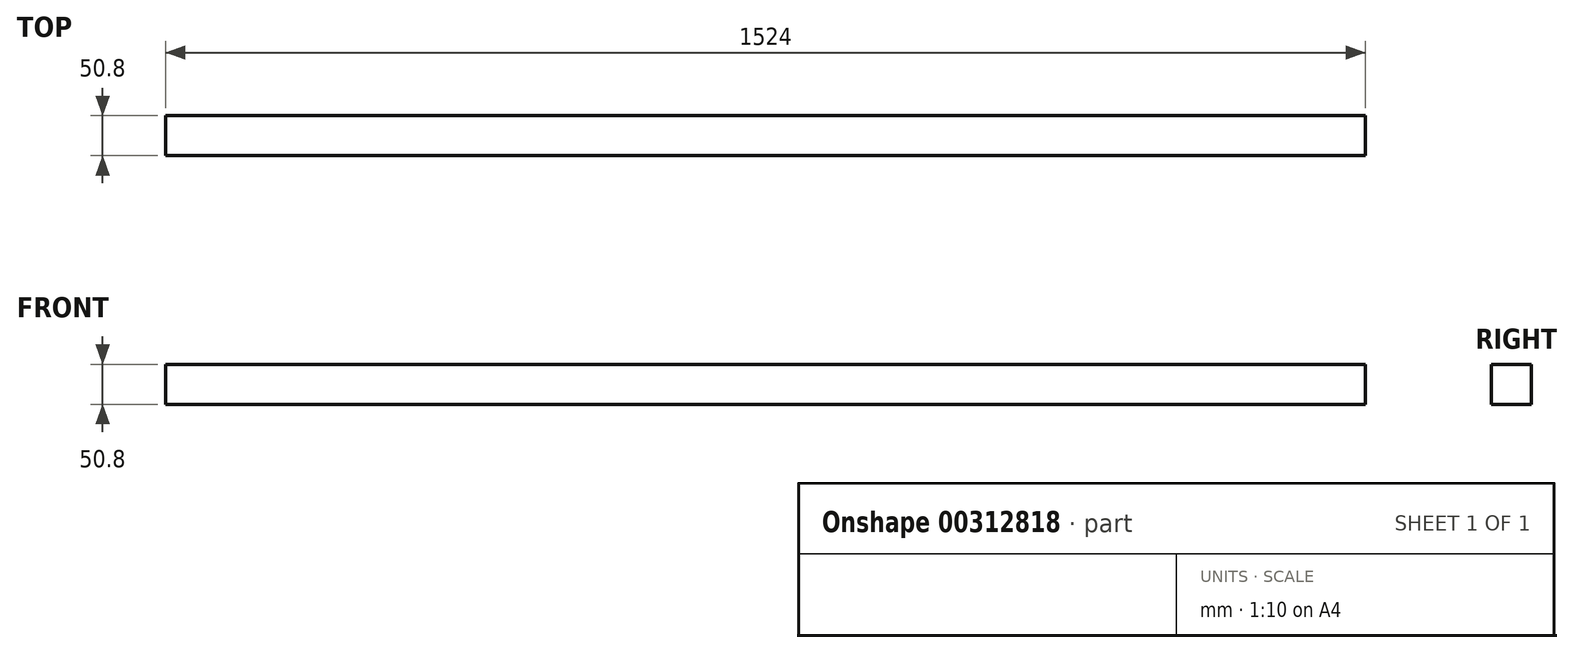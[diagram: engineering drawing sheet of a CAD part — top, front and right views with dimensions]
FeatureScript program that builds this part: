
annotation { "Feature Type Name" : "Feature", "Feature Type Description" : "" }
export const myFeature = defineFeature(function(context is Context, id is Id, definition is map)
    precondition{}
    {
        {
            var Q0;
            Q0=qCreatedBy(makeId("Top.planeOp"),FACE);
            var sketch = newSketch(context, id + "F0", { "sketchPlane" : qUnion([Q0])});
            skLineSegment(sketch, "E0.bottom", {"start": v(-754.72, -135.2) * mm, "end": v(769.28, -135.2) * mm});
            skLineSegment(sketch, "E0.top", {"start": v(-754.72, -186) * mm, "end": v(769.28, -186) * mm});
            skLineSegment(sketch, "E0.left", {"start": v(-754.72, -135.2) * mm, "end": v(-754.72, -186) * mm});
            skLineSegment(sketch, "E0.right", {"start": v(769.28, -135.2) * mm, "end": v(769.28, -186) * mm});
            skSolve(sketch);
        }
        {
            var Q0;
            Q0=makeQuery(id+"F0.imprint","IMPRINT",FACE,{"disambiguationData":[TD([[makeQuery(id+"F0.imprint","IMPRINT",EDGE,{"derivedFrom":sQuery(id+"F0.wireOp",EDGE,"E0.bottom")}),-1.0]])]});
            extrude(context, id + "F1", {"entities" : qUnion([Q0]), "depth" : 50.8 * mm});
        }
    });
